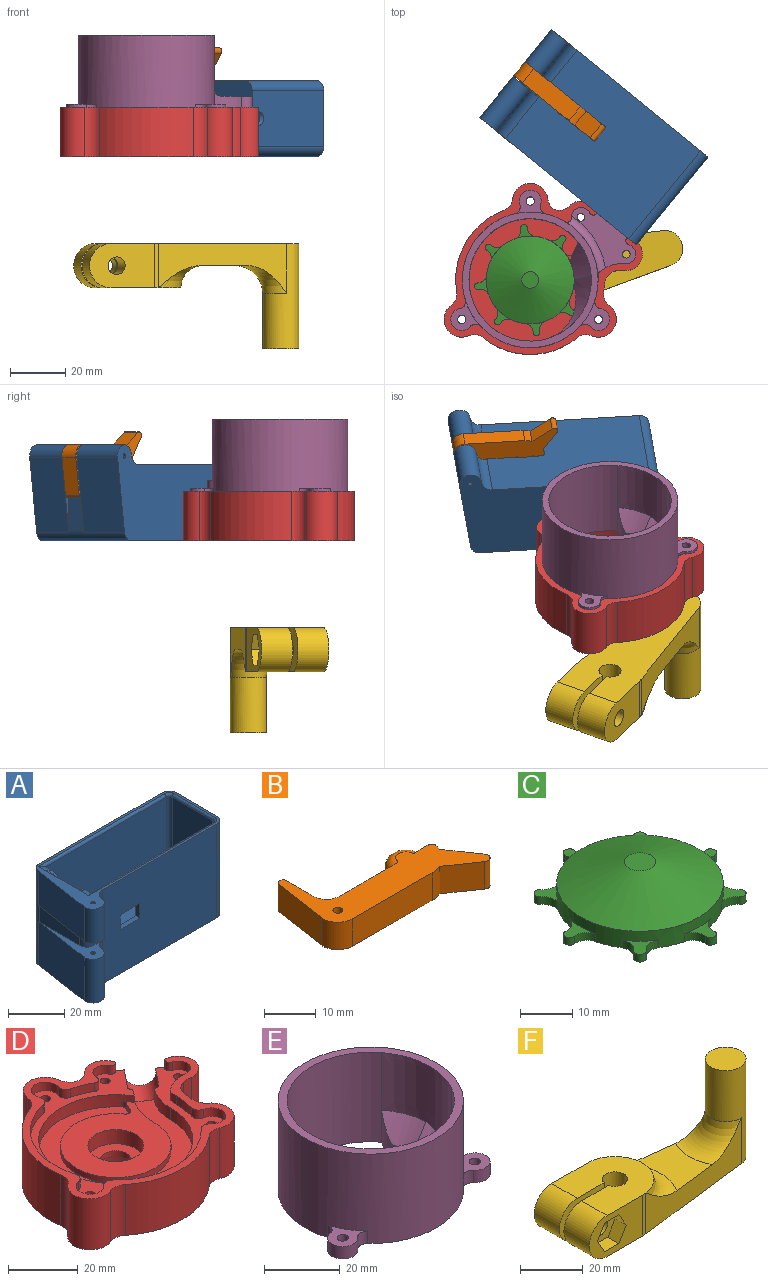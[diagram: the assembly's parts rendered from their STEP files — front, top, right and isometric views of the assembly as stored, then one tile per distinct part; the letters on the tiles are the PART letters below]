
ASSEMBLY  parts=6 mates=11
PART A: 56 faces, bbox 73x34.6x41 mm
  f0: plane 27.06x19mm, normal (-0.99,0.15,0), area 519.7mm2, adj f2,f6,f47,f55
  f1: cylinder r=4mm len=19mm, axis (0,0,-1), area 111.1mm2, adj f2,f5,f47,f55
  f2: cylinder r=4mm len=19mm, axis (0,0,-1), area 241.6mm2, adj f0,f1,f47,f55
  f3: cylinder r=0.79mm len=19mm, axis (0,0,-1), area 94.8mm2, adj f47,f55
  f4: cylinder r=0.79mm len=15mm, axis (0,0,-1), area 74.8mm2, adj f25,f54
  f5: plane 62x41mm, normal (0,-1,0), area 2325.6mm2, adj f1,f9,f10,f25,f31,f32,f33,f34
  f6: cylinder r=3.5mm len=41mm, axis (0,0,-1), area 208mm2, adj f0,f8,f13,f25,f47,f52,f54,f55
  f7: plane 60.95x29mm, normal (0,1,0), area 1668.8mm2, adj f21,f22,f26,f31,f32,f33,f34,f37
  f8: plane 20.5x7mm, normal (-1,0,0), area 143.5mm2, adj f6,f9,f54,f55
  f9: cylinder r=3.5mm len=7mm, axis (0,0,-1), area 38.5mm2, adj f5,f8,f54,f55
  f10: cylinder r=3.5mm len=41mm, axis (0,0,-1), area 225.4mm2, adj f5,f11,f25,f47
  f11: plane 41x20.5mm, normal (1,0,0), area 821.6mm2, adj f10,f12,f25,f47,f53
  f12: cylinder r=3.5mm len=41mm, axis (0,0,-1), area 225.4mm2, adj f11,f13,f25,f47
  f13: plane 62x41mm, normal (0,1,0), area 2542mm2, adj f6,f12,f25,f47
  f14: plane 30x19mm, normal (1,0,0), area 351mm2, adj f15,f24,f25,f26,f35,f38
  f15: plane 26.25x2.25mm, normal (0,-1,0), area 59.1mm2, adj f14,f16,f26,f38
  f16: cylinder r=1.5mm len=26.25mm, axis (0,0,-1), area 61.9mm2, adj f15,f17,f26,f39
  f17: plane 26.25x4.5mm, normal (1,0,0), area 118.1mm2, adj f16,f18,f26,f40
  f18: plane 60.95x29mm, normal (0,-1,0), area 1733.8mm2, adj f17,f19,f26,f40,f45
  f19: cylinder r=1.5mm len=29mm, axis (0,0,-1), area 68.3mm2, adj f18,f20,f26,f44
  f20: plane 29x20.5mm, normal (-1,0,0), area 594.5mm2, adj f19,f21,f26,f43
  f21: cylinder r=1.5mm len=29mm, axis (0,0,-1), area 68.3mm2, adj f7,f20,f26,f42
  f22: plane 26.25x4.5mm, normal (1,0,0), area 118.1mm2, adj f7,f23,f26,f37
  f23: cylinder r=1.5mm len=26.25mm, axis (0,0,-1), area 61.9mm2, adj f22,f24,f26,f36
  f24: plane 26.25x2.25mm, normal (0,1,0), area 59.1mm2, adj f14,f23,f26,f35
  f25: plane 73x34.63mm, normal (0,0,1), area 303.6mm2, adj f4,f5,f6,f10,f11,f12,f13,f14
  f26: plane 65x23.5mm, normal (0,0,1), area 934.4mm2, adj f7,f14,f15,f16,f17,f18,f19,f20
  f27: cylinder r=6.75mm len=13.5mm, axis (0,0,1), area 63.6mm2, adj f26,f28,f30,f46
  f28: plane 30x3mm, normal (0,-1,0), area 90mm2, adj f26,f27,f29,f46
  f29: cylinder r=6.75mm len=13.5mm, axis (0,0,1), area 63.6mm2, adj f26,f28,f30,f46
  f30: plane 30x3mm, normal (0,1,0), area 90mm2, adj f26,f27,f29,f46
  f31: plane 10x2mm, normal (0,0,1), area 20mm2, adj f5,f7,f32,f33
  f32: plane 6.5x2mm, normal (1,0,0), area 13mm2, adj f5,f7,f31,f34
  f33: plane 6.5x2mm, normal (-1,0,0), area 13mm2, adj f5,f7,f31,f34
  f34: plane 10x2mm, normal (0,0,-1), area 20mm2, adj f5,f7,f32,f33
  f35: cylinder r=3.75mm len=3.75mm, axis (1,0,0), area 8.4mm2, adj f14,f24,f36
  f36: bspline ~4.43x3.75mm, area 9.4mm2, adj f23,f35,f37
  f37: cylinder r=3.75mm len=5.5mm, axis (0,-1,0), area 22.8mm2, adj f7,f22,f25,f36,f41
  f38: cylinder r=3.75mm len=3.75mm, axis (-1,0,0), area 8.4mm2, adj f14,f15,f39
  f39: bspline ~4.43x3.75mm, area 9.4mm2, adj f16,f38,f40
  f40: cylinder r=3.75mm len=5.5mm, axis (0,-1,0), area 22.8mm2, adj f17,f18,f25,f39,f45
  f41: cylinder r=1mm len=63.5mm, axis (1,0,0), area 97.6mm2, adj f7,f25,f37,f42
  f42: torus R=2.5mm, axis (0,0,1), area 4.6mm2, adj f21,f25,f41,f43
  f43: cylinder r=1mm len=20.5mm, axis (0,1,0), area 32.2mm2, adj f20,f25,f42,f44
  f44: torus R=2.5mm, axis (0,0,1), area 4.6mm2, adj f19,f25,f43,f45
  f45: cylinder r=1mm len=63.5mm, axis (-1,0,0), area 97.6mm2, adj f18,f25,f40,f44
  f46: plane 43.5x13.5mm, normal (0,0,1), area 497.9mm2, adj f27,f28,f29,f30,f48
  f47: plane 73x34.63mm, normal (0,0,-1), area 1933.7mm2, adj f0,f1,f2,f3,f5,f6,f10,f11
  f48: cylinder r=4mm len=8mm, axis (0,0,1), area 194.3mm2, adj f46,f47,f49
  f49: cylinder r=1.45mm len=6.52mm, axis (1,0,0), area 58.2mm2, adj f48,f53
  f50: cylinder r=4mm len=15mm, axis (0,0,-1), area 87.7mm2, adj f5,f25,f51,f54
  f51: cylinder r=4mm len=15mm, axis (0,0,-1), area 190.8mm2, adj f25,f50,f52,f54
  f52: plane 27.06x15mm, normal (-0.99,0.15,0), area 410.3mm2, adj f6,f25,f51,f54
  f53: cone r=1.45mm half-angle=45deg, axis (1,0,0), area 17.3mm2, adj f11,f49
  f54: plane 31.64x11.95mm, normal (0,0,-1), area 96.9mm2, adj f4,f5,f6,f8,f9,f50,f51,f52
  f55: plane 31.64x11.95mm, normal (0,0,1), area 96.9mm2, adj f0,f1,f2,f3,f5,f6,f8,f9
PART B: 20 faces, bbox 37.6x23.8x6.5 mm
  f0: plane 37.63x23.77mm, normal (0,0,1), area 292.8mm2, adj f1,f2,f3,f4,f5,f6,f7,f8
  f1: plane 13.58x6.5mm, normal (-0.99,0.15,0), area 89.3mm2, adj f0,f2,f12,f17
  f2: cylinder r=4mm len=6.5mm, axis (0,0,-1), area 44.7mm2, adj f0,f1,f3,f12
  f3: plane 21.75x6.5mm, normal (0,-1,0), area 141.4mm2, adj f0,f2,f4,f12
  f4: cylinder r=7.13mm len=6.5mm, axis (0,0,-1), area 17.3mm2, adj f0,f3,f5,f12
  f5: plane 7.29x6.5mm, normal (-0.57,-0.82,0), area 57.5mm2, adj f0,f4,f6,f12
  f6: cylinder r=1.27mm len=6.5mm, axis (0,0,-1), area 22.9mm2, adj f0,f5,f7,f12
  f7: plane 7.29x6.5mm, normal (0.82,0.57,0), area 57.5mm2, adj f0,f6,f8,f12
  f8: cylinder r=7.13mm len=6.5mm, axis (0,0,-1), area 9.7mm2, adj f0,f7,f9,f12
  f9: cylinder r=1mm len=6.5mm, axis (0,0,-1), area 11.3mm2, adj f0,f8,f10,f12
  f10: plane 6.5x4.05mm, normal (0,1,0), area 15mm2, adj f0,f9,f11,f12,f18,f19
  f11: cylinder r=4mm len=8mm, axis (0,0,-1), area 31.4mm2, adj f10,f14,f18,f19
  f12: plane 37.63x23.77mm, normal (0,0,-1), area 292.8mm2, adj f1,f2,f3,f4,f5,f6,f7,f8
  f13: cylinder r=0.95mm len=6.5mm, axis (0,0,-1), area 38.9mm2, adj f0,f12
  f14: plane 16.25x6.5mm, normal (0,1,0), area 94.3mm2, adj f0,f11,f12,f16,f18,f19
  f15: plane 6.88x6.5mm, normal (1,0,0), area 44.7mm2, adj f0,f12,f16,f17
  f16: cylinder r=3.5mm len=6.5mm, axis (0,0,-1), area 39.1mm2, adj f0,f12,f14,f15
  f17: cylinder r=1mm len=6.5mm, axis (0,0,1), area 19.5mm2, adj f0,f1,f12,f15
  f18: torus R=2mm, axis (0,0,1), area 32.3mm2, adj f0,f10,f11,f14
  f19: torus R=2mm, axis (0,0,1), area 32.3mm2, adj f10,f11,f12,f14
PART C: 40 faces, bbox 40.5x40.5x9.1 mm
  f0: plane 40.46x40.46mm, normal (0,0,-1), area 851.2mm2, adj f8,f9,f10,f11,f12,f13,f14,f15
  f1: plane 6.24x6.24mm, normal (0,0,1), area 12.4mm2, adj f8,f15,f16,f17
  f2: plane 7.18x4.74mm, normal (0,0,1), area 12.4mm2, adj f8,f18,f19,f20
  f3: plane 6.24x6.24mm, normal (0,0,1), area 12.4mm2, adj f8,f21,f22,f23
  f4: plane 7.18x4.74mm, normal (0,0,1), area 12.4mm2, adj f8,f24,f25,f26
  f5: plane 6.24x6.24mm, normal (0,0,1), area 12.4mm2, adj f8,f27,f28,f29
  f6: plane 7.18x4.74mm, normal (0,0,1), area 12.4mm2, adj f8,f30,f31,f32
  f7: plane 7.18x4.74mm, normal (0,0,1), area 12.4mm2, adj f12,f13,f14,f34
  f8: cylinder r=15.91mm len=31.81mm, axis (0,0,-1), area 291.1mm2, adj f0,f1,f2,f3,f4,f5,f6,f9
  f9: cylinder r=3.12mm len=4.1mm, axis (0,0,-1), area 8.2mm2, adj f0,f8,f10,f33
  f10: cylinder r=1.2mm len=2.14mm, axis (0,0,-1), area 7.3mm2, adj f0,f9,f11,f33
  f11: cylinder r=3.12mm len=4.1mm, axis (0,0,-1), area 8.2mm2, adj f0,f8,f10,f33
  f12: cylinder r=3.12mm len=3.4mm, axis (0,0,-1), area 8.2mm2, adj f0,f7,f8,f13
  f13: cylinder r=1.2mm len=2.4mm, axis (0,0,-1), area 7.3mm2, adj f0,f7,f12,f14
  f14: cylinder r=3.12mm len=3.4mm, axis (0,0,-1), area 8.2mm2, adj f0,f7,f8,f13
  f15: cylinder r=3.12mm len=4.1mm, axis (0,0,-1), area 8.2mm2, adj f0,f1,f8,f16
  f16: cylinder r=1.2mm len=2.14mm, axis (0,0,-1), area 7.3mm2, adj f0,f1,f15,f17
  f17: cylinder r=3.12mm len=4.1mm, axis (0,0,-1), area 8.2mm2, adj f0,f1,f8,f16
  f18: cylinder r=3.12mm len=3.4mm, axis (0,0,-1), area 8.2mm2, adj f0,f2,f8,f19
  f19: cylinder r=1.2mm len=2.4mm, axis (0,0,-1), area 7.3mm2, adj f0,f2,f18,f20
  f20: cylinder r=3.12mm len=3.4mm, axis (0,0,-1), area 8.2mm2, adj f0,f2,f8,f19
  f21: cylinder r=3.12mm len=4.1mm, axis (0,0,-1), area 8.2mm2, adj f0,f3,f8,f22
  f22: cylinder r=1.2mm len=2.14mm, axis (0,0,-1), area 7.3mm2, adj f0,f3,f21,f23
  f23: cylinder r=3.12mm len=4.1mm, axis (0,0,-1), area 8.2mm2, adj f0,f3,f8,f22
  f24: cylinder r=3.12mm len=3.4mm, axis (0,0,-1), area 8.2mm2, adj f0,f4,f8,f25
  f25: cylinder r=1.2mm len=2.4mm, axis (0,0,-1), area 7.3mm2, adj f0,f4,f24,f26
  f26: cylinder r=3.12mm len=3.4mm, axis (0,0,-1), area 8.2mm2, adj f0,f4,f8,f25
  f27: cylinder r=3.12mm len=4.1mm, axis (0,0,-1), area 8.2mm2, adj f0,f5,f8,f28
  f28: cylinder r=1.2mm len=2.14mm, axis (0,0,-1), area 7.3mm2, adj f0,f5,f27,f29
  f29: cylinder r=3.12mm len=4.1mm, axis (0,0,-1), area 8.2mm2, adj f0,f5,f8,f28
  f30: cylinder r=3.12mm len=3.4mm, axis (0,0,-1), area 8.2mm2, adj f0,f6,f8,f31
  f31: cylinder r=1.2mm len=2.4mm, axis (0,0,-1), area 7.3mm2, adj f0,f6,f30,f32
  f32: cylinder r=3.12mm len=3.4mm, axis (0,0,-1), area 8.2mm2, adj f0,f6,f8,f31
  f33: plane 6.24x6.24mm, normal (0,0,1), area 12.4mm2, adj f8,f9,f10,f11
  f34: extruded ~7.18x2.33mm, area 16.8mm2, adj f7,f8,f39
  f35: plane 6.55x4.13mm, normal (-1,0,0), area 27mm2, adj f0,f36,f37
  f36: cylinder r=4mm len=8mm, axis (0,0,-1), area 72.1mm2, adj f0,f35,f37
  f37: plane 8x6.3mm, normal (0,0,-1), area 42.5mm2, adj f35,f36
  f38: plane 6x6mm, normal (0,0,1), area 28.3mm2, adj f39
  f39: cone r=3mm half-angle=68.8deg, axis (0,0,-1), area 793.5mm2, adj f8,f34,f38
PART D: 67 faces, bbox 71.8x61.9x17.9 mm
  f0: plane 0.79x0.02mm, normal (0.63,0.78,0), area 0mm2, adj f8,f63
  f1: plane 0.61x0.5mm, normal (0.63,0.78,0), area 0mm2, adj f9,f63
  f2: plane 66.96x57.11mm, normal (0,0,1), area 649.2mm2, adj f4,f8,f10,f11,f12,f13,f14,f15
  f3: cylinder r=4.5mm len=9mm, axis (0,0,-1), area 56.5mm2, adj f19,f20
  f4: cylinder r=22.16mm len=14.53mm, axis (0,0,1), area 38mm2, adj f2,f5,f9,f13,f18,f61,f63
  f5: cylinder r=15.91mm len=31.81mm, axis (0,0,1), area 179.9mm2, adj f4,f9,f18,f64
  f6: cylinder r=24.56mm len=3mm, axis (0,0,-1), area 6.7mm2, adj f9,f18,f64,f65
  f7: cylinder r=8mm len=16mm, axis (0,0,1), area 251.3mm2, adj f18,f19
  f8: cylinder r=15.91mm len=10.6mm, axis (0,0,1), area 46.7mm2, adj f0,f2,f9,f13,f63
  f9: plane 48.36x44.31mm, normal (0,0,1), area 758.6mm2, adj f1,f4,f5,f6,f8,f13,f63,f64
  f10: cylinder r=1.5mm len=14.88mm, axis (0,0,-1), area 140.2mm2, adj f2,f66
  f11: cylinder r=1.5mm len=14.88mm, axis (0,0,-1), area 140.2mm2, adj f2,f66
  f12: cylinder r=1.5mm len=14.88mm, axis (0,0,-1), area 140.2mm2, adj f2,f66
  f13: cylinder r=22.16mm len=44.31mm, axis (0,0,1), area 533.6mm2, adj f2,f4,f8,f9,f18,f65
  f14: plane 14.88x11.19mm, normal (0.63,0.78,0), area 170.4mm2, adj f2,f41,f49,f62,f66
  f15: cylinder r=1.4mm len=14.88mm, axis (0,0,-1), area 130.8mm2, adj f2,f66
  f16: cylinder r=1.4mm len=14.88mm, axis (0,0,-1), area 130.8mm2, adj f2,f66
  f17: cylinder r=8mm len=16mm, axis (0,0,-1), area 282.7mm2, adj f20,f66
  f18: plane 34.94x31.81mm, normal (0,0,1), area 616.8mm2, adj f4,f5,f6,f7,f13,f64,f65
  f19: plane 16x16mm, normal (0,0,1), area 137.4mm2, adj f3,f7
  f20: plane 16x16mm, normal (0,0,-1), area 137.4mm2, adj f3,f17
  f21: cylinder r=3.5mm len=6.87mm, axis (0,0,-1), area 31.2mm2, adj f2,f32,f33,f50
  f22: cylinder r=4mm len=7.94mm, axis (0,0,-1), area 46mm2, adj f2,f23,f36,f50
  f23: cylinder r=2.5mm len=3.74mm, axis (0,0,-1), area 12.7mm2, adj f2,f22,f24,f50
  f24: cylinder r=24.56mm len=35.88mm, axis (0,0,-1), area 120.7mm2, adj f2,f23,f25,f50
  f25: cylinder r=2.5mm len=3.74mm, axis (0,0,-1), area 12.7mm2, adj f2,f24,f26,f50
  f26: cylinder r=4mm len=7.94mm, axis (0,0,-1), area 46mm2, adj f2,f25,f27,f50
  f27: cylinder r=2.5mm len=3.19mm, axis (0,0,-1), area 12.7mm2, adj f2,f26,f28,f50
  f28: cylinder r=24.56mm len=31.07mm, axis (0,0,-1), area 120.7mm2, adj f2,f27,f29,f50
  f29: cylinder r=2.5mm len=3.28mm, axis (0,0,-1), area 12.7mm2, adj f2,f28,f30,f50
  f30: cylinder r=4mm len=8mm, axis (0,0,-1), area 46mm2, adj f2,f29,f37,f50
  f31: cylinder r=3.5mm len=6.61mm, axis (0,0,-1), area 28.7mm2, adj f2,f39,f40,f50
  f32: cylinder r=1.5mm len=3mm, axis (0,0,-1), area 8.5mm2, adj f2,f21,f50,f51
  f33: cylinder r=12mm len=9.57mm, axis (0,0,-1), area 31.3mm2, adj f2,f21,f34,f50
  f34: cylinder r=13.51mm len=3mm, axis (0,0,-1), area 7.7mm2, adj f2,f33,f35,f50
  f35: cylinder r=24.56mm len=7.15mm, axis (0,0,-1), area 21.8mm2, adj f2,f34,f36,f50
  f36: cylinder r=2.5mm len=3.19mm, axis (0,0,-1), area 12.7mm2, adj f2,f22,f35,f50
  f37: cylinder r=2.5mm len=3.28mm, axis (0,0,-1), area 12.7mm2, adj f2,f30,f38,f50
  f38: cylinder r=24.56mm len=7.07mm, axis (0,0,-1), area 23mm2, adj f2,f37,f39,f50
  f39: cylinder r=1.5mm len=3mm, axis (0,0,-1), area 9.8mm2, adj f2,f31,f38,f50
  f40: cylinder r=1.5mm len=3mm, axis (0,0,-1), area 8.5mm2, adj f2,f31,f50,f52
  f41: cylinder r=5.9mm len=17.88mm, axis (0,0,-1), area 220.9mm2, adj f14,f50,f52,f54,f66
  f42: cylinder r=6.4mm len=17.88mm, axis (0,0,-1), area 332.7mm2, adj f50,f53,f55,f66
  f43: cylinder r=26.96mm len=29.54mm, axis (0,0,-1), area 660.1mm2, adj f50,f55,f56,f66
  f44: cylinder r=6.4mm len=17.88mm, axis (0,0,-1), area 332.7mm2, adj f50,f56,f57,f66
  f45: cylinder r=26.96mm len=34.11mm, axis (0,0,-1), area 660.1mm2, adj f50,f57,f58,f66
  f46: cylinder r=6.4mm len=17.88mm, axis (0,0,-1), area 332.7mm2, adj f50,f58,f59,f66
  f47: cylinder r=26.96mm len=17.88mm, axis (0,0,-1), area 53mm2, adj f50,f59,f60,f66
  f48: cylinder r=9.6mm len=17.88mm, axis (0,0,-1), area 63.7mm2, adj f49,f50,f60,f66
  f49: cylinder r=5.9mm len=17.88mm, axis (0,0,-1), area 333.4mm2, adj f14,f48,f50,f51,f66
  f50: plane 71.76x61.91mm, normal (0,0,1), area 532.4mm2, adj f21,f22,f23,f24,f25,f26,f27,f28
  f51: cylinder r=0.5mm len=3mm, axis (0,0,1), area 1.4mm2, adj f2,f32,f49,f50
  f52: cylinder r=0.5mm len=3mm, axis (0,0,1), area 1.4mm2, adj f2,f40,f41,f50
  f53: cylinder r=5mm len=17.88mm, axis (0,0,1), area 90.9mm2, adj f42,f50,f54,f66
  f54: cylinder r=5mm len=17.88mm, axis (0,0,1), area 95.5mm2, adj f41,f50,f53,f66
  f55: cylinder r=5mm len=17.88mm, axis (0,0,1), area 97.6mm2, adj f42,f43,f50,f66
  f56: cylinder r=5mm len=17.88mm, axis (0,0,1), area 97.6mm2, adj f43,f44,f50,f66
  f57: cylinder r=5mm len=17.88mm, axis (0,0,1), area 97.6mm2, adj f44,f45,f50,f66
  f58: cylinder r=5mm len=17.88mm, axis (0,0,1), area 97.6mm2, adj f45,f46,f50,f66
  f59: cylinder r=5mm len=17.88mm, axis (0,0,1), area 97.6mm2, adj f46,f47,f50,f66
  f60: cylinder r=5mm len=17.88mm, axis (0,0,-1), area 111.9mm2, adj f47,f48,f50,f66
  f61: plane 0.79x0.02mm, normal (0.63,0.78,0), area 0mm2, adj f4,f63
  f62: cylinder r=4.65mm len=12.58mm, axis (0.63,0.78,0), area 143.5mm2, adj f2,f14,f63
  f63: torus R=3.15mm, axis (0.63,0.78,0), area 31.4mm2, adj f0,f1,f2,f4,f8,f9,f61,f62
  f64: cylinder r=1.5mm len=2.59mm, axis (0,0,1), area 6.3mm2, adj f5,f6,f9,f18
  f65: cylinder r=1.5mm len=2mm, axis (0,0,-1), area 3.7mm2, adj f6,f9,f13,f18
  f66: plane 71.76x61.91mm, normal (0,0,-1), area 2645.4mm2, adj f10,f11,f12,f14,f15,f16,f17,f41
PART E: 48 faces, bbox 67.7x62x30.4 mm
  f0: cylinder r=22.16mm len=44.31mm, axis (0,0,-1), area 3257mm2, adj f28,f30,f31,f33,f36,f37,f43,f44
  f1: plane 11.19x9.12mm, normal (0.63,0.78,0), area 77.4mm2, adj f10,f11,f30,f38,f39
  f2: cylinder r=24.56mm len=49.11mm, axis (0,0,-1), area 4086.9mm2, adj f3,f4,f6,f14,f15,f17,f18,f20
  f3: plane 11.1x8.64mm, normal (0,0,1), area 50.2mm2, adj f2,f15,f16,f17,f27
  f4: plane 11.13x10.79mm, normal (0,0,1), area 50.2mm2, adj f2,f18,f19,f20,f26
  f5: cylinder r=22.16mm len=10.73mm, axis (0,0,-1), area 23.4mm2, adj f30,f31,f41,f42
  f6: cylinder r=13.51mm len=10mm, axis (0,0,-1), area 23.9mm2, adj f2,f7,f30,f47
  f7: cylinder r=12mm len=9.57mm, axis (0,0,-1), area 75.5mm2, adj f6,f8,f30,f38,f47
  f8: cylinder r=3.5mm len=7mm, axis (0,0,-1), area 72.8mm2, adj f7,f9,f30,f38
  f9: cylinder r=1.5mm len=7mm, axis (0,0,-1), area 19.9mm2, adj f8,f10,f30,f38
  f10: cylinder r=0.5mm len=7mm, axis (0,0,-1), area 3.2mm2, adj f1,f9,f30,f38
  f11: cylinder r=0.5mm len=7mm, axis (0,0,-1), area 3.2mm2, adj f1,f12,f30,f38
  f12: cylinder r=1.5mm len=7mm, axis (0,0,-1), area 19.9mm2, adj f11,f13,f30,f38
  f13: cylinder r=3.5mm len=7.07mm, axis (0,0,-1), area 66.9mm2, adj f12,f14,f30,f38,f47
  f14: cylinder r=1.5mm len=10mm, axis (0,0,-1), area 27.8mm2, adj f2,f13,f30,f47
  f15: cylinder r=2.5mm len=4mm, axis (0,0,-1), area 16.9mm2, adj f2,f3,f16,f30
  f16: cylinder r=4mm len=8mm, axis (0,0,-1), area 61.3mm2, adj f3,f15,f17,f30
  f17: cylinder r=2.5mm len=4mm, axis (0,0,-1), area 16.9mm2, adj f2,f3,f16,f30
  f18: cylinder r=2.5mm len=4mm, axis (0,0,-1), area 16.9mm2, adj f2,f4,f19,f30
  f19: cylinder r=4mm len=7.94mm, axis (0,0,-1), area 61.3mm2, adj f4,f18,f20,f30
  f20: cylinder r=2.5mm len=4mm, axis (0,0,-1), area 16.9mm2, adj f2,f4,f19,f30
  f21: cylinder r=2.5mm len=4mm, axis (0,0,-1), area 16.9mm2, adj f2,f22,f30,f35
  f22: cylinder r=4mm len=7.94mm, axis (0,0,-1), area 61.3mm2, adj f21,f23,f30,f35
  f23: cylinder r=2.5mm len=4mm, axis (0,0,-1), area 16.9mm2, adj f2,f22,f30,f35
  f24: cylinder r=1.4mm len=7mm, axis (0,0,-1), area 61.6mm2, adj f30,f38
  f25: cylinder r=1.5mm len=4mm, axis (0,0,-1), area 37.7mm2, adj f30,f35
  f26: cylinder r=1.5mm len=4mm, axis (0,0,-1), area 37.7mm2, adj f4,f30
  f27: cylinder r=1.5mm len=4mm, axis (0,0,-1), area 37.7mm2, adj f3,f30
  f28: cylinder r=15.91mm len=10.6mm, axis (0,0,-1), area 22.5mm2, adj f0,f30,f31,f41
  f29: cylinder r=1.4mm len=7mm, axis (0,0,-1), area 61.6mm2, adj f30,f38
  f30: plane 67.2x57.35mm, normal (0,0,-1), area 669.2mm2, adj f0,f1,f2,f5,f6,f7,f8,f9
  f31: plane 33.38x14.16mm, normal (0,0,-1), area 138.4mm2, adj f0,f5,f28,f32,f34,f40,f41,f42
  f32: cylinder r=22.16mm len=4.17mm, axis (0,0,-1), area 4.3mm2, adj f31,f34,f43,f44,f45
  f33: cylinder r=24.56mm len=10.4mm, axis (0,0,-1), area 54.8mm2, adj f0,f30,f34,f46
  f34: cylinder r=15.91mm len=6.68mm, axis (0,0,-1), area 21mm2, adj f30,f31,f32,f33,f42,f46
  f35: plane 11.13x10.79mm, normal (0,0,1), area 50.2mm2, adj f2,f21,f22,f23,f25
  f36: extruded ~24.86x22.8mm, area 519.9mm2, adj f0,f37,f45,f46
  f37: plane 49.11x49.11mm, normal (0,0,1), area 352.2mm2, adj f0,f2,f36
  f38: plane 23.32x21.81mm, normal (0,0,1), area 202mm2, adj f1,f7,f8,f9,f10,f11,f12,f13
  f39: cylinder r=4.65mm len=12.37mm, axis (0.63,0.78,0), area 104.9mm2, adj f1,f30,f41
  f40: plane 0.61x0.5mm, normal (0.63,0.78,0), area 0mm2, adj f31,f41
  f41: torus R=3.15mm, axis (-0.63,-0.78,0), area 19.1mm2, adj f5,f28,f30,f31,f39,f40
  f42: cylinder r=0.4mm len=2mm, axis (0,0,-1), area 2.2mm2, adj f5,f30,f31,f34
  f43: cylinder r=15mm len=17.45mm, axis (0,0,-1), area 9.2mm2, adj f0,f32,f44,f45
  f44: cone r=15.8mm half-angle=45deg, axis (0,0,-1), area 23.9mm2, adj f0,f31,f32,f43
  f45: cone r=15.8mm half-angle=45deg, axis (0,0,1), area 122.1mm2, adj f0,f32,f36,f43,f46
  f46: bspline ~16.25x9.74mm, area 86.8mm2, adj f33,f34,f36,f45
  f47: torus R=27.56mm, axis (0,0,1), area 106.8mm2, adj f2,f6,f7,f13,f14,f38
PART F: 27 faces, bbox 80.5x56.3x38 mm
  f0: cylinder r=3.17mm len=6.5mm, axis (0,-1,0), area 129.7mm2, adj f7,f26
  f1: cylinder r=12.5mm len=16mm, axis (0,0,-1), area 24.1mm2, adj f3,f4,f12,f15
  f2: plane 20.92x18.09mm, normal (0,0,1), area 273.4mm2, adj f3,f10,f14,f16
  f3: plane 49.28x18mm, normal (0.12,0.99,0), area 493.7mm2, adj f1,f2,f11,f12,f14,f16
  f4: plane 24x16mm, normal (0,1,0), area 324.9mm2, adj f1,f12,f15,f17,f19
  f5: plane 20.13x16mm, normal (0,-1,0), area 262.9mm2, adj f6,f12,f15,f17,f19
  f6: cylinder r=4mm len=16mm, axis (0,0,-1), area 369.8mm2, adj f5,f7,f12,f15
  f7: plane 20.13x16mm, normal (0,1,0), area 262.9mm2, adj f0,f6,f12,f15,f18
  f8: plane 24x16mm, normal (0,-1,0), area 246.9mm2, adj f9,f12,f15,f18,f20,f21,f22,f23
  f9: cylinder r=12.5mm len=16mm, axis (0,0,-1), area 24.1mm2, adj f8,f10,f12,f15
  f10: plane 49.28x18mm, normal (0.12,-0.99,0), area 493.7mm2, adj f2,f9,f11,f12,f14,f16
  f11: cylinder r=6.5mm len=38mm, axis (0,0,-1), area 1156.2mm2, adj f3,f10,f12,f13,f14
  f12: plane 72.5x25mm, normal (0,0,-1), area 1348.9mm2, adj f1,f3,f4,f5,f6,f7,f8,f9
  f13: plane 13x13mm, normal (0,0,1), area 132.7mm2, adj f11
  f14: torus R=16.5mm, axis (0,0,1), area 275.8mm2, adj f2,f3,f10,f11
  f15: plane 28.5x25mm, normal (0,0,1), area 571.1mm2, adj f1,f4,f5,f6,f7,f8,f9,f16
  f16: torus R=20.5mm, axis (0,0,1), area 340.6mm2, adj f2,f3,f10,f15
  f17: cylinder r=3.17mm len=11.5mm, axis (0,-1,0), area 229.4mm2, adj f4,f5
  f18: cylinder r=8mm len=16mm, axis (0,-1,0), area 289mm2, adj f7,f8,f12,f15
  f19: cylinder r=8mm len=16mm, axis (0,-1,0), area 289mm2, adj f4,f5,f12,f15
  f20: plane 5.63x5mm, normal (-0.87,0,-0.5), area 32.5mm2, adj f8,f21,f25,f26
  f21: plane 6.5x5mm, normal (0,0,-1), area 32.5mm2, adj f8,f20,f22,f26
  f22: plane 5.63x5mm, normal (0.87,0,-0.5), area 32.5mm2, adj f8,f21,f23,f26
  f23: plane 5.63x5mm, normal (0.87,0,0.5), area 32.5mm2, adj f8,f22,f24,f26
  f24: plane 6.5x5mm, normal (0,0,1), area 32.5mm2, adj f8,f23,f25,f26
  f25: plane 5.63x5mm, normal (-0.87,0,0.5), area 32.5mm2, adj f8,f20,f24,f26
  f26: plane 12.99x11.25mm, normal (0,-1,0), area 77.9mm2, adj f0,f20,f21,f22,f23,f24,f25
PLACE A rot(axis=(-0.89,0.32,-0.32),96.5deg) t=(16.67,40.67,9)mm
PLACE B rot(axis=(-0.89,0.32,-0.32),96.5deg) t=(16.83,40.86,9)mm
PLACE C rot(axis=(0,0,-1),38.1deg) t=(0,0,67.87)mm
PLACE D t=(0,0,-3)mm fixed
PLACE E t=(0,0,-3)mm
PLACE F rot(axis=(0.99,0.12,0),180deg) t=(0,0,-36.2)mm
MATE cylindrical E.f0 <-> D.f43  axis (0,0,-1) through (0,0,24.63)mm
MATE cylindrical A.f48 <-> D.f62  axis (0.63,0.78,0) through (32.16,22.88,9)mm
MATE planar B.f0 <-> A.f2  axis (0.63,0.78,0) through (9.74,69.55,29.88)mm
MATE planar E.f0 <-> D.f28  axis (0,0,-1) through (0,0,10.13)mm
MATE cylindrical E.f16 <-> D.f10  axis (0,0,-1) through (0,28.56,12.13)mm
MATE cylindrical C.f36 <-> D.f3  axis (0,0,-1) through (0,0,9.94)mm
MATE planar B.f14 <-> A.f5  axis (0,0,-1) through (7.59,67.1,22.75)mm
MATE cylindrical F.f6 <-> D.f3  axis (0,0,1) through (0,0,-44.2)mm
MATE planar C.f0 <-> D.f18  axis (0,0,-1) through (0.02,-0.02,7.88)mm
MATE cylindrical B.f2 <-> A.f2  axis (-0.63,-0.78,0) through (-0.75,73.9,25.88)mm
MATE planar A.f47 <-> D.f14  axis (-0.63,-0.78,0) through (9.79,35.96,9.59)mm
